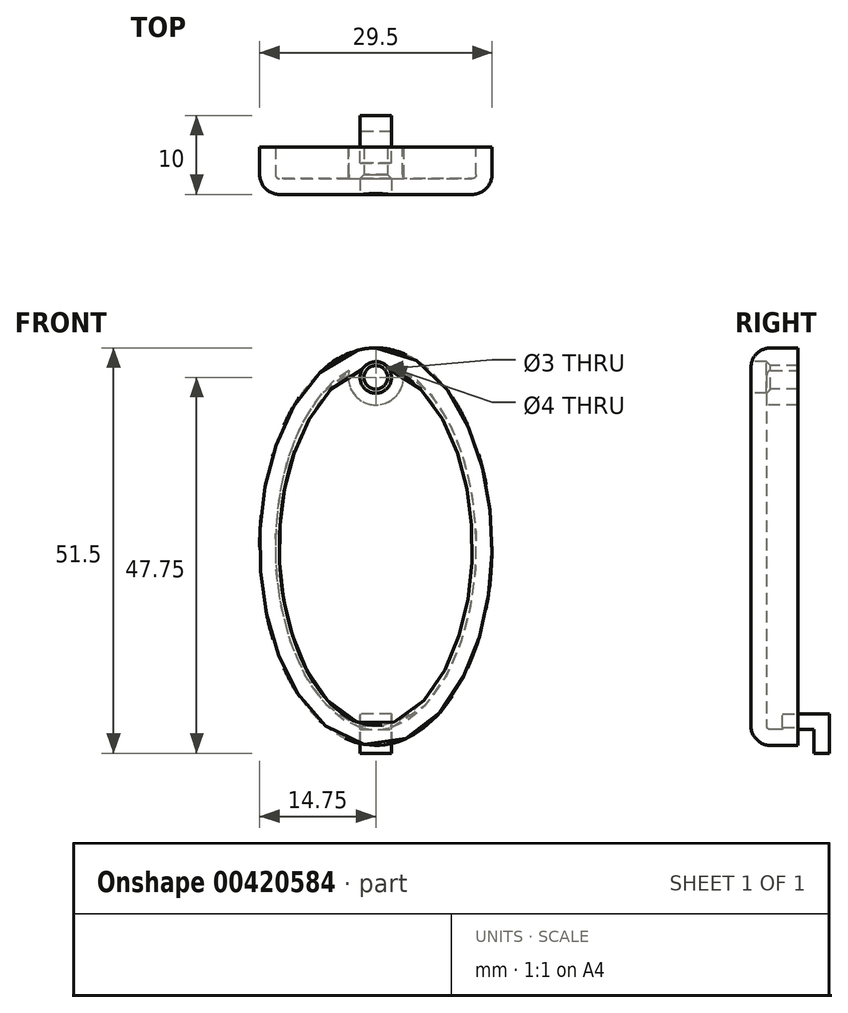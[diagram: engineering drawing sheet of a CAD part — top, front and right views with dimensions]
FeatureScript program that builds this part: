
annotation { "Feature Type Name" : "Feature", "Feature Type Description" : "" }
export const myFeature = defineFeature(function(context is Context, id is Id, definition is map)
    precondition{}
    {
        {
            var Q0;
            Q0=qCreatedBy(makeId("Front.planeOp"),FACE);
            var sketch = newSketch(context, id + "F0", { "sketchPlane" : qUnion([Q0])});
            skEllipse(sketch, "E0", {"center": v(0, 0) * mm, "majorRadius": 25.25 * mm, "minorRadius": 14.75 * mm, "majorAxis": v(0, 1)});
            skSolve(sketch);
        }
        {
            var Q0;
            Q0 = qSketchRegion(id + "F0", true);
            extrude(context, id + "F1", {"entities" : qUnion([Q0]), "depth" : 6 * mm, "offsetDistance" : 25 * mm});
        }
        {
            var Q0;
            Q0=makeQuery(id+"F1.opExtrude","CAP_EDGE",EDGE,{"disambiguationData":[OSD([sQuery(id+"F0.wireOp",EDGE,"E0")])],"isStart":false});
            fillet(context, id + "F2", {"entities" : qUnion([Q0]), "radius" : 2.5 * mm, "tangentPropagation" : true, "allowEdgeOverflow" : false});
        }
        {
            var Q0;
            Q0=makeQuery(id+"F1.opExtrude","CAP_FACE",FACE,{"disambiguationData":[OSD([sQuery(id+"F0.wireOp",EDGE,"E0")])],"isStart":false});
            var sketch = newSketch(context, id + "F3", { "sketchPlane" : qUnion([Q0])});
            skCircle(sketch, "E1", {"center": v(0, 21.5) * mm, "radius": 1.5 * mm});
            skSolve(sketch);
        }
        {
            var Q0;
            Q0 = qSketchRegion(id + "F3", true);
            extrude(context, id + "F4", {"entities" : qUnion([Q0]), "operationType" : NewBodyOperationType.REMOVE, "endBound" : BoundingType.THROUGH_ALL, "oppositeDirection" : true, "depth" : 25 * mm, "offsetDistance" : 25 * mm});
        }
        {
            var Q0;
            Q0=makeQuery(id+"F1.opExtrude","CAP_FACE",FACE,{"disambiguationData":[OSD([sQuery(id+"F0.wireOp",EDGE,"E0")])],"isStart":true});
            shell(context, id + "F5", {"entities" : qUnion([Q0]), "thickness" : 2 * mm});
        }
        {
            var Q0;
            Q0=qCreatedBy(makeId("Right.planeOp"),FACE);
            var sketch = newSketch(context, id + "F6", { "sketchPlane" : qUnion([Q0])});
            skLineSegment(sketch, "E2", {"start": v(-2, -23.25) * mm, "end": v(-2, -21.25) * mm});
            skLineSegment(sketch, "E3", {"start": v(-2, -21.25) * mm, "end": v(4, -21.25) * mm});
            skLineSegment(sketch, "E4", {"start": v(4, -21.25) * mm, "end": v(4, -26.25) * mm});
            skLineSegment(sketch, "E5", {"start": v(4, -26.25) * mm, "end": v(2, -26.25) * mm});
            skLineSegment(sketch, "E6", {"start": v(2, -26.25) * mm, "end": v(2, -23.25) * mm});
            skLineSegment(sketch, "E7", {"start": v(2, -23.25) * mm, "end": v(-2, -23.25) * mm});
            skSolve(sketch);
        }
        {
            var Q0;
            Q0 = qSketchRegion(id + "F6", true);
            extrude(context, id + "F7", {"entities" : qUnion([Q0]), "operationType" : NewBodyOperationType.ADD, "depth" : 4 * mm, "offsetDistance" : 25 * mm, "symmetric" : true});
        }
        {
            var Q0;
            Q0=makeQuery(id+"F1.opExtrude","CAP_FACE",FACE,{"disambiguationData":[OSD([sQuery(id+"F0.wireOp",EDGE,"E0")])],"isStart":false});
            var sketch = newSketch(context, id + "F8", { "sketchPlane" : qUnion([Q0])});
            skCircle(sketch, "E8", {"center": v(0, 21.5) * mm, "radius": 2 * mm});
            skSolve(sketch);
        }
        {
            var Q0;
            Q0 = qSketchRegion(id + "F8", true);
            extrude(context, id + "F9", {"entities" : qUnion([Q0]), "operationType" : NewBodyOperationType.REMOVE, "oppositeDirection" : true, "depth" : 2 * mm, "offsetDistance" : 25 * mm});
        }
        {
            var Q0;
            Q0=makeQuery(id+"F9.boolean.opBoolean","INTERSECT",EDGE,{"derivedFrom":[makeQuery(id+"F4.boolean.opBoolean","COPY",FACE,{"derivedFrom":makeQuery(id+"F4.opExtrude","SWEPT_FACE",FACE,{"disambiguationData":[OSD([sQuery(id+"F3.wireOp",EDGE,"E1")])]})}),makeQuery(id+"F9.opExtrude","CAP_FACE",FACE,{"disambiguationData":[OSD([sQuery(id+"F8.wireOp",EDGE,"E8")])],"isStart":false})]});
            chamfer(context, id + "F10", {"entities" : qUnion([Q0]), "width" : 0.5 * mm, "tangentPropagation" : true});
        }
    });
